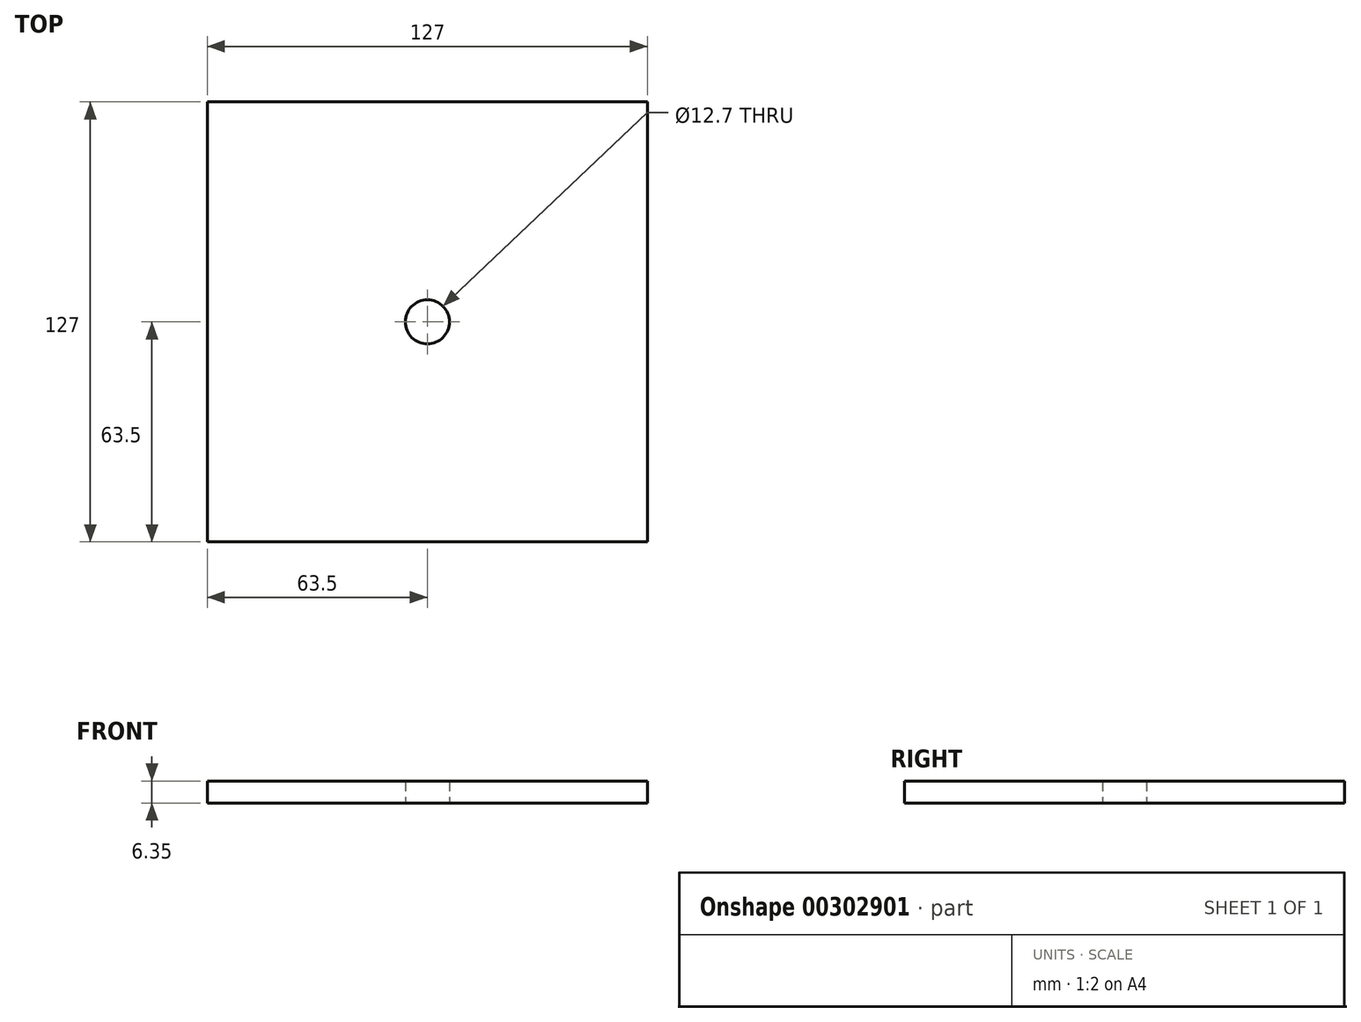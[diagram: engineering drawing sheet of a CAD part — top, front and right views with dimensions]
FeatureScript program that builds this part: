
annotation { "Feature Type Name" : "Feature", "Feature Type Description" : "" }
export const myFeature = defineFeature(function(context is Context, id is Id, definition is map)
    precondition{}
    {
        {
            var Q0;
            Q0=qCreatedBy(makeId("Top.planeOp"),FACE);
            var sketch = newSketch(context, id + "F0", { "sketchPlane" : qUnion([Q0])});
            skLineSegment(sketch, "E0.bottom", {"start": v(63.5, 63.5) * mm, "end": v(-63.5, 63.5) * mm});
            skLineSegment(sketch, "E0.top", {"start": v(63.5, -63.5) * mm, "end": v(-63.5, -63.5) * mm});
            skLineSegment(sketch, "E0.left", {"start": v(63.5, 63.5) * mm, "end": v(63.5, -63.5) * mm});
            skLineSegment(sketch, "E0.right", {"start": v(-63.5, 63.5) * mm, "end": v(-63.5, -63.5) * mm});
            skPoint(sketch, "E0.middle", {"position": v(0, 0) * mm});
            skCircle(sketch, "E1", {"center": v(0, 0) * mm, "radius": 6.35 * mm});
            skSolve(sketch);
        }
        {
            var Q0;
            Q0=makeQuery(id+"F0.imprint","IMPRINT",FACE,{"disambiguationData":[TD([[makeQuery(id+"F0.imprint","IMPRINT",EDGE,{"derivedFrom":sQuery(id+"F0.wireOp",EDGE,"E0.bottom")}),1.0]])]});
            extrude(context, id + "F1", {"entities" : qUnion([Q0]), "depth" : 6.35 * mm});
        }
    });
